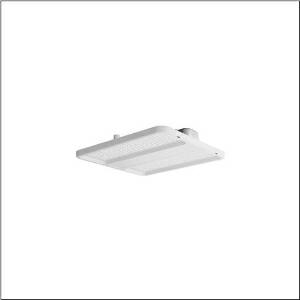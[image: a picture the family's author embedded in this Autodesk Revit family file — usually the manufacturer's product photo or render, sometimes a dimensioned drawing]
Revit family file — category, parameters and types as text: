
# Revit family: highbay_11_midi_51hn12da4mda
name_source: partatom
category: Lighting Fixtures
units: mm (PartAtom-declared; Revit-internal decimal feet)

## family parameters
Cut with Voids When Loaded = No
Host = Face
Light Source = No
Part Type = Normal
Room Calculation Point = No
Round Connector Dimension = Use Diameter
Shared = No

## types (1)
- --- (1 x LED, 4530 lm, 22.2 W, 4000K)
    Apparent Load = 22 VA
    CIE Flux Codes = 87 98 100 100 100
    Color Rendering = 80
    Color Temperature = 4000K
    Default Elevation = 1800 mm
    Description = high bay luminaire Highbay 11 midi; direct symmetric wide distribution, light control with lens of PMMA; UGR ≤ 22 (X = 4H | Y = 8H | S = 0.25H | reflection values 70/50/20); luminous flux: 28.000lm; light colour: 840, colour temperature: 4000K, MacAdam ≤ 2 SDCM (initial), colour rendering: CRI > 80; luminous efficacy: 191lm/W; rated service life: 100.000h (L95/B50) at AT= 25°C; control: DALI 2; housing frame of high-performance plastic PA6, matt traffic white (RAL 9016); cover of PMMA; dimension (LxWxH): 474 x 442 x 72mm; luminaire connection: terminal, 5-pole, max. 2.5mm² (cable entry for one cable, Ø 8.5..16mm); mains connection: 230..240V, AC/DC 0/50..60Hz; connected load: 146,6W; protection rating (complete): IP66; insulation class (complete): insulation class I (protective earthing); protection symbol: D; impact resistance: IK08; halogen-free wiring; for central battery installations according to DIN EN 60598-2-22; corresponds to IFS (International Featured Standards) requirements for safety and quality in the food industry; LABS conformity tested according to VDMA 24364:2018-05; certification: CE, ENEC, VDE, UKCA; permissible operating ambient temperature: -40..+50°C (reducing of maximum allowable ambient temperature of 5°C with ceiling mounting); packaging unit: 1 piece; (delivery without accessories; please order mounting accessories separately)
    Height = 72 mm  [stored 0.23622 ft]
    Lamp = 1 x LED
    Lamp Light Flux = 4530 lm
    Lamp Power = 22.2 W
    Lamp count = 1
    Length = 474 mm
    Luminous efficacy = 204 lm/W
    Manufacturer = Siteco
    ModVariant = No
    Model = 51HN12DA4MDA
    Mounting Place = Ceiling
    Mounting Type = Pendant
    Number of Poles = 1
    OnlyDefault = Yes
    Power Factor = 1
    Product Name = Highbay 11 midi
    Product group = high bay luminaire
    ProductGroupID = 901
    Protection Class = Protection class I
    Protection Degree = IP 66
    RLX_Detail_Level = 1
    RLX_Emergency_Light_Flux = 0 lm
    RLX_Emergency_Type = 0
    RLX_Emergency_Type_DB = No
    RlxData = <blob elided: 16813 chars, md5=998561b7>
    Socket = socket
    Standby Power = 0 W
    System Light Flux = 4530 lm
    System Power = 22 W
    Type Comments = : DC mode (central or group accumulator) initial emergency light level
    Type Image = l_1363240.jpg
    URL = http://relux.com
    VarID = @adj_005181
    Voltage = 0 V
    Weight = 0.00 kg
    Width = 442 mm

note: [stored X ft] marks values corroborated as IEEE doubles in the binary element streams (Revit-internal decimal feet)

## geometry (parser evidence)
native form markers: Blend x4, Sweep x11
no freeform markers — native parametric forms only
